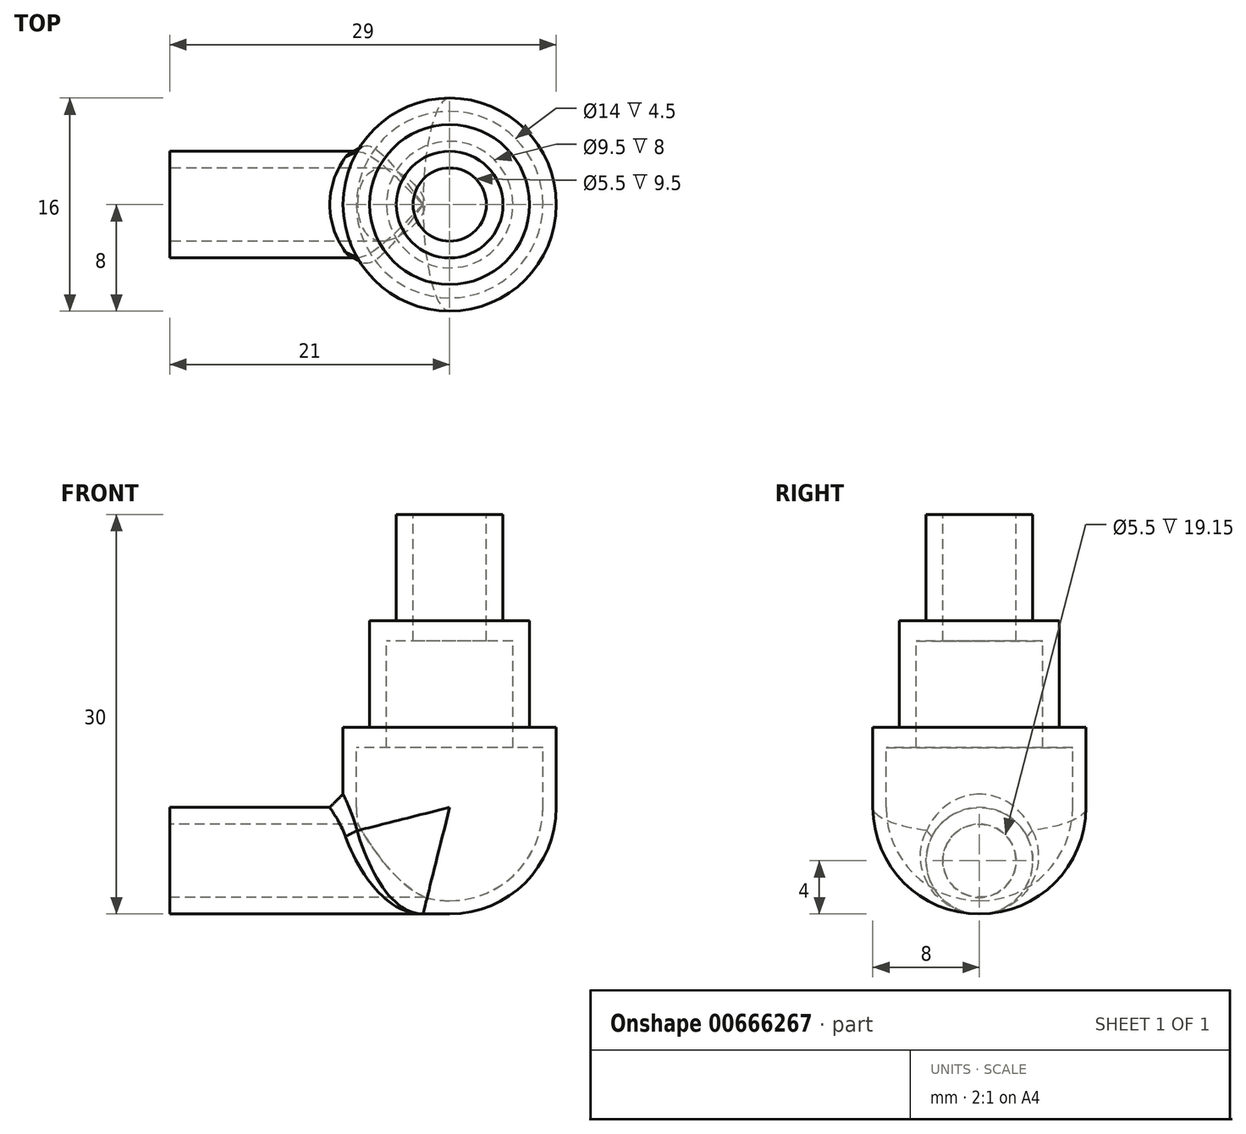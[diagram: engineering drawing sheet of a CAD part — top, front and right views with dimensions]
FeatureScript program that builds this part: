
annotation { "Feature Type Name" : "Feature", "Feature Type Description" : "" }
export const myFeature = defineFeature(function(context is Context, id is Id, definition is map)
    precondition{}
    {
        {
            var Q0;
            Q0=qCreatedBy(makeId("Front.planeOp"),FACE);
            var sketch = newSketch(context, id + "F0", { "sketchPlane" : qUnion([Q0])});
            skArc(sketch, "E0", {"start": v(0, -6) * mm, "mid": v(4.24, -4.24) * mm, "end": v(6, 0) * mm});
            skLineSegment(sketch, "E1", {"start": v(0, -6) * mm, "end": v(-15, -6) * mm});
            skLineSegment(sketch, "E2", {"start": v(6, 0) * mm, "end": v(6, 20) * mm});
            skSolve(sketch);
        }
        {
            var Q0;
            Q0=qCreatedBy(makeId("Right.planeOp"),FACE);
            var Q1;
            Q1=sQuery(id+"F0.wireOp",VERTEX,"E1.end");
            cPlane(context, id + "F1", {"entities" : qUnion([Q0, Q1]), "cplaneType" : CPlaneType.PLANE_POINT, "offset" : 25 * mm, "width" : 150 * mm, "height" : 150 * mm});
        }
        {
            var Q0;
            Q0=qCreatedBy(id+"F1.planeOp",FACE);
            var sketch = newSketch(context, id + "F2", { "sketchPlane" : qUnion([Q0])});
            skCircle(sketch, "E3", {"center": v(0, -6) * mm, "radius": 3 * mm, "construction": true});
            skCircle(sketch, "E4", {"center": v(0, -6) * mm, "radius": 4 * mm});
            skSolve(sketch);
        }
        {
            var Q0;
            Q0=makeQuery(id+"F2.imprint","IMPRINT",FACE,{"disambiguationData":[TD([[makeQuery(id+"F2.imprint","IMPRINT",EDGE,{"derivedFrom":sQuery(id+"F2.wireOp",EDGE,"E4")}),1.0]])]});
            var Q1;
            Q1=sQuery(id+"F0.wireOp",EDGE,"E1");
            var Q2;
            Q2=sQuery(id+"F0.wireOp",EDGE,"E0");
            var Q3;
            Q3=sQuery(id+"F0.wireOp",EDGE,"E2");
            sweep(context, id + "F3", {"profiles" : qUnion([Q0]), "path" : qUnion([Q1, Q2, Q3])});
        }
        {
            var Q0;
            Q0=qCreatedBy(makeId("Front.planeOp"),FACE);
            var sketch = newSketch(context, id + "F4", { "sketchPlane" : qUnion([Q0])});
            skLineSegment(sketch, "E5", {"start": v(15.78, 4) * mm, "end": v(-2, 4) * mm, "construction": true});
            skLineSegment(sketch, "E6", {"start": v(-2, 4) * mm, "end": v(-2, -10) * mm});
            skLineSegment(sketch, "E7", {"start": v(-2, -10) * mm, "end": v(6, -10) * mm});
            skLineSegment(sketch, "E8", {"start": v(-2, 4) * mm, "end": v(0, 4) * mm});
            skLineSegment(sketch, "E9", {"start": v(0, 4) * mm, "end": v(0, 12) * mm});
            skLineSegment(sketch, "E10", {"start": v(0, 12) * mm, "end": v(6, 12) * mm});
            skLineSegment(sketch, "E11", {"start": v(6, 12) * mm, "end": v(6, -10) * mm});
            skSolve(sketch);
        }
        {
            var Q0;
            Q0 = qSketchRegion(id + "F4", true);
            var Q1;
            Q1=sQuery(id+"F0.wireOp",EDGE,"E2");
            revolve(context, id + "F5", {"operationType" : NewBodyOperationType.ADD, "surfaceOperationType" : NewSurfaceOperationType.NEW, "entities" : qUnion([Q0]), "axis" : qUnion([Q1]), "revolveType" : RevolveType.FULL});
        }
        {
            var Q0;
            Q0=qCreatedBy(makeId("Front.planeOp"),FACE);
            var sketch = newSketch(context, id + "F6", { "sketchPlane" : qUnion([Q0])});
            skLineSegment(sketch, "E12", {"start": v(14, 2) * mm, "end": v(14, 12.91) * mm, "construction": true});
            skLineSegment(sketch, "E13", {"start": v(-13.64, -10) * mm, "end": v(6, -10) * mm, "construction": true});
            skLineSegment(sketch, "E14", {"start": v(6, -10) * mm, "end": v(14, -10) * mm});
            skLineSegment(sketch, "E15", {"start": v(14, -10) * mm, "end": v(14, 2) * mm, "construction": true});
            skLineSegment(sketch, "E16", {"start": v(14, 2) * mm, "end": v(19, 2) * mm});
            skLineSegment(sketch, "E17", {"start": v(19, 2) * mm, "end": v(19, -10) * mm});
            skLineSegment(sketch, "E18", {"start": v(19, -10) * mm, "end": v(14, -10) * mm});
            skLineSegment(sketch, "E19", {"start": v(14, 2) * mm, "end": v(14, -2) * mm});
            skArc(sketch, "E20", {"start": v(6, -10) * mm, "mid": v(11.66, -7.66) * mm, "end": v(14, -2) * mm});
            skSolve(sketch);
        }
        {
            var Q0;
            Q0=makeQuery(id+"F6.imprint","IMPRINT",FACE,{"disambiguationData":[TD([[makeQuery(id+"F6.imprint","IMPRINT",EDGE,{"derivedFrom":sQuery(id+"F6.wireOp",EDGE,"E14")}),1.0]])]});
            var Q1;
            Q1=sQuery(id+"F0.wireOp",EDGE,"E2");
            revolve(context, id + "F7", {"operationType" : NewBodyOperationType.REMOVE, "surfaceOperationType" : NewSurfaceOperationType.NEW, "entities" : qUnion([Q0]), "axis" : qUnion([Q1]), "revolveType" : RevolveType.SYMMETRIC, "oppositeDirection" : true, "angle" : 180 * degree});
        }
        {
            var Q0;
            Q0=makeQuery(id+"F7.boolean.opBoolean","COPY",FACE,{"derivedFrom":makeQuery(id+"F7.opRevolve","CAP_FACE",FACE,{"disambiguationData":[OSD([sQuery(id+"F6.wireOp",EDGE,"E14"),sQuery(id+"F6.wireOp",EDGE,"E16"),sQuery(id+"F6.wireOp",EDGE,"E17"),sQuery(id+"F6.wireOp",EDGE,"E18"),sQuery(id+"F6.wireOp",EDGE,"E19"),sQuery(id+"F6.wireOp",EDGE,"E20")])],"isStart":false})});
            var Q1;
            Q1=makeQuery(id+"F7.boolean.opBoolean","COPY",FACE,{"derivedFrom":makeQuery(id+"F7.opRevolve","CAP_FACE",FACE,{"disambiguationData":[OSD([sQuery(id+"F6.wireOp",EDGE,"E14"),sQuery(id+"F6.wireOp",EDGE,"E16"),sQuery(id+"F6.wireOp",EDGE,"E17"),sQuery(id+"F6.wireOp",EDGE,"E18"),sQuery(id+"F6.wireOp",EDGE,"E19"),sQuery(id+"F6.wireOp",EDGE,"E20")])],"isStart":true})});
            extrude(context, id + "F8", {"entities" : qUnion([Q0, Q1]), "operationType" : NewBodyOperationType.REMOVE, "endBound" : BoundingType.THROUGH_ALL, "oppositeDirection" : true, "depth" : 25 * mm, "offsetDistance" : 25 * mm});
        }
        {
            var Q0;
            {var subQ0=sQuery(id+"F6.wireOp",EDGE,"E20");Q0=makeQuery(id+"F8.boolean.opBoolean","INTERSECT",EDGE,{"derivedFrom":[makeQuery(id+"F5.opRevolve","SWEPT_FACE",FACE,{"disambiguationData":[OSD([sQuery(id+"F4.wireOp",EDGE,"E6")])]}),makeQuery(id+"F8.opExtrude","SWEPT_FACE",FACE,{"disambiguationData":[OSD([subQ0]),TDD([makeQuery(id+"F7.boolean.opBoolean","COPY",EDGE,{"derivedFrom":makeQuery(id+"F7.opRevolve","CAP_EDGE",EDGE,{"disambiguationData":[OSD([subQ0])],"isStart":false})})])]})]});}
            fillet(context, id + "F9", {"entities" : qUnion([Q0]), "radius" : 6 * mm, "tangentPropagation" : true, "allowEdgeOverflow" : false});
        }
        {
            var Q0;
            Q0=qCreatedBy(makeId("Front.planeOp"),FACE);
            var sketch = newSketch(context, id + "F10", { "sketchPlane" : qUnion([Q0])});
            skLineSegment(sketch, "E21", {"start": v(6, 2.5) * mm, "end": v(13, 2.5) * mm, "construction": true});
            skLineSegment(sketch, "E22", {"start": v(13, 2.5) * mm, "end": v(13, -2) * mm});
            skLineSegment(sketch, "E23", {"start": v(6, -9) * mm, "end": v(6, 2.5) * mm});
            skArc(sketch, "E24", {"start": v(6, -9) * mm, "mid": v(10.95, -6.95) * mm, "end": v(13, -2) * mm});
            skLineSegment(sketch, "E25", {"start": v(6, -9) * mm, "end": v(-3.68, -9) * mm, "construction": true});
            skLineSegment(sketch, "E26", {"start": v(6, 2.5) * mm, "end": v(6, 20) * mm});
            skLineSegment(sketch, "E27", {"start": v(6, 20) * mm, "end": v(8.75, 20) * mm});
            skLineSegment(sketch, "E28", {"start": v(8.75, 20) * mm, "end": v(8.75, 10.5) * mm});
            skLineSegment(sketch, "E29", {"start": v(8.75, 10.5) * mm, "end": v(10.75, 10.5) * mm});
            skLineSegment(sketch, "E30", {"start": v(10.75, 10.5) * mm, "end": v(10.75, 2.5) * mm});
            skLineSegment(sketch, "E31", {"start": v(10.75, 2.5) * mm, "end": v(13, 2.5) * mm});
            skSolve(sketch);
        }
        {
            var Q0;
            Q0 = qSketchRegion(id + "F10", true);
            var Q1;
            Q1=sQuery(id+"F0.wireOp",EDGE,"E2");
            revolve(context, id + "F11", {"operationType" : NewBodyOperationType.REMOVE, "surfaceOperationType" : NewSurfaceOperationType.NEW, "entities" : qUnion([Q0]), "axis" : qUnion([Q1]), "revolveType" : RevolveType.FULL, "oppositeDirection" : true});
        }
        {
            var Q0;
            Q0=makeQuery(id+"F3.opSweep","CAP_FACE",FACE,{"disambiguationData":[OSD([sQuery(id+"F0.wireOp",VERTEX,"E1.end"),sQuery(id+"F2.wireOp",EDGE,"E4")])],"isStart":true});
            var sketch = newSketch(context, id + "F12", { "sketchPlane" : qUnion([Q0])});
            skCircle(sketch, "E32", {"center": v(0, -6) * mm, "radius": 2.75 * mm});
            skSolve(sketch);
        }
        {
            var Q0;
            Q0 = qSketchRegion(id + "F12", true);
            var Q1;
            Q1=makeQuery(id+"F11.boolean.opBoolean","COPY",FACE,{"derivedFrom":makeQuery(id+"F11.opRevolve","SWEPT_FACE",FACE,{"disambiguationData":[OSD([sQuery(id+"F10.wireOp",EDGE,"E24")])]})});
            extrude(context, id + "F13", {"entities" : qUnion([Q0]), "operationType" : NewBodyOperationType.REMOVE, "endBound" : BoundingType.UP_TO_SURFACE, "oppositeDirection" : true, "depth" : 25 * mm, "endBoundEntityFace" : qUnion([Q1]), "offsetDistance" : 25 * mm});
        }
        {
            var Q0;
            Q0=makeQuery(id+"F5.boolean.opBoolean","INTERSECT",EDGE,{"derivedFrom":[makeQuery(id+"F3.opSweep","SWEPT_FACE",FACE,{"disambiguationData":[OSD([sQuery(id+"F0.wireOp",EDGE,"E1"),sQuery(id+"F2.wireOp",EDGE,"E4")])]}),makeQuery(id+"F5.opRevolve","SWEPT_FACE",FACE,{"disambiguationData":[OSD([sQuery(id+"F4.wireOp",EDGE,"E6")])]})]});
            chamfer(context, id + "F14", {"entities" : qUnion([Q0]), "width" : 1 * mm, "tangentPropagation" : true});
        }
    });
